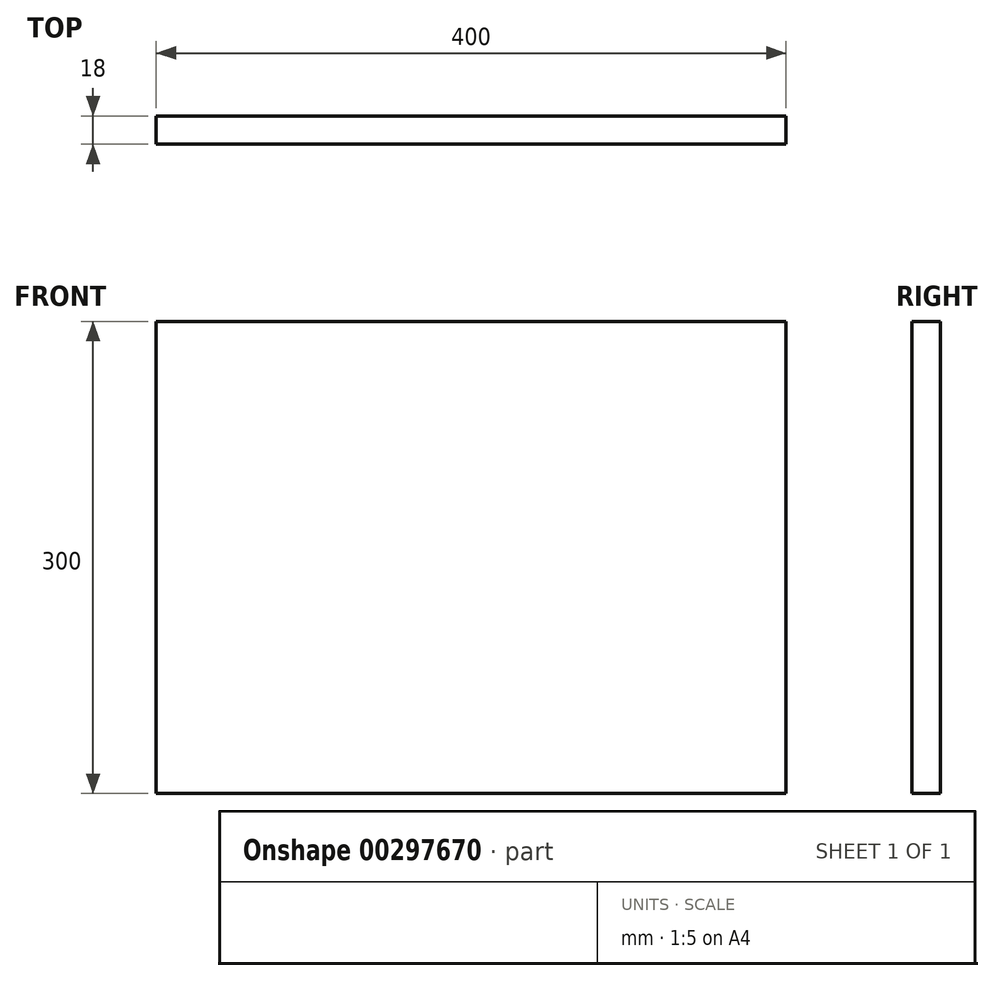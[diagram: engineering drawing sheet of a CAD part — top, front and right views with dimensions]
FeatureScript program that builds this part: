
annotation { "Feature Type Name" : "Feature", "Feature Type Description" : "" }
export const myFeature = defineFeature(function(context is Context, id is Id, definition is map)
    precondition{}
    {
        {
            var Q0;
            Q0=qCreatedBy(makeId("Front.planeOp"),FACE);
            var sketch = newSketch(context, id + "F0", { "sketchPlane" : qUnion([Q0])});
            skLineSegment(sketch, "E0.bottom", {"start": v(-158.06, 274.84) * mm, "end": v(241.94, 274.84) * mm});
            skLineSegment(sketch, "E0.top", {"start": v(-158.06, -25.16) * mm, "end": v(241.94, -25.16) * mm});
            skLineSegment(sketch, "E0.left", {"start": v(-158.06, 274.84) * mm, "end": v(-158.06, -25.16) * mm});
            skLineSegment(sketch, "E0.right", {"start": v(241.94, 274.84) * mm, "end": v(241.94, -25.16) * mm});
            skSolve(sketch);
        }
        {
            var Q0;
            Q0=makeQuery(id+"F0.imprint","IMPRINT",FACE,{"disambiguationData":[TD([[makeQuery(id+"F0.imprint","IMPRINT",EDGE,{"derivedFrom":sQuery(id+"F0.wireOp",EDGE,"E0.bottom")}),-1.0]])]});
            extrude(context, id + "F1", {"entities" : qUnion([Q0]), "depth" : 18 * mm, "offsetDistance" : 25 * mm});
        }
    });
